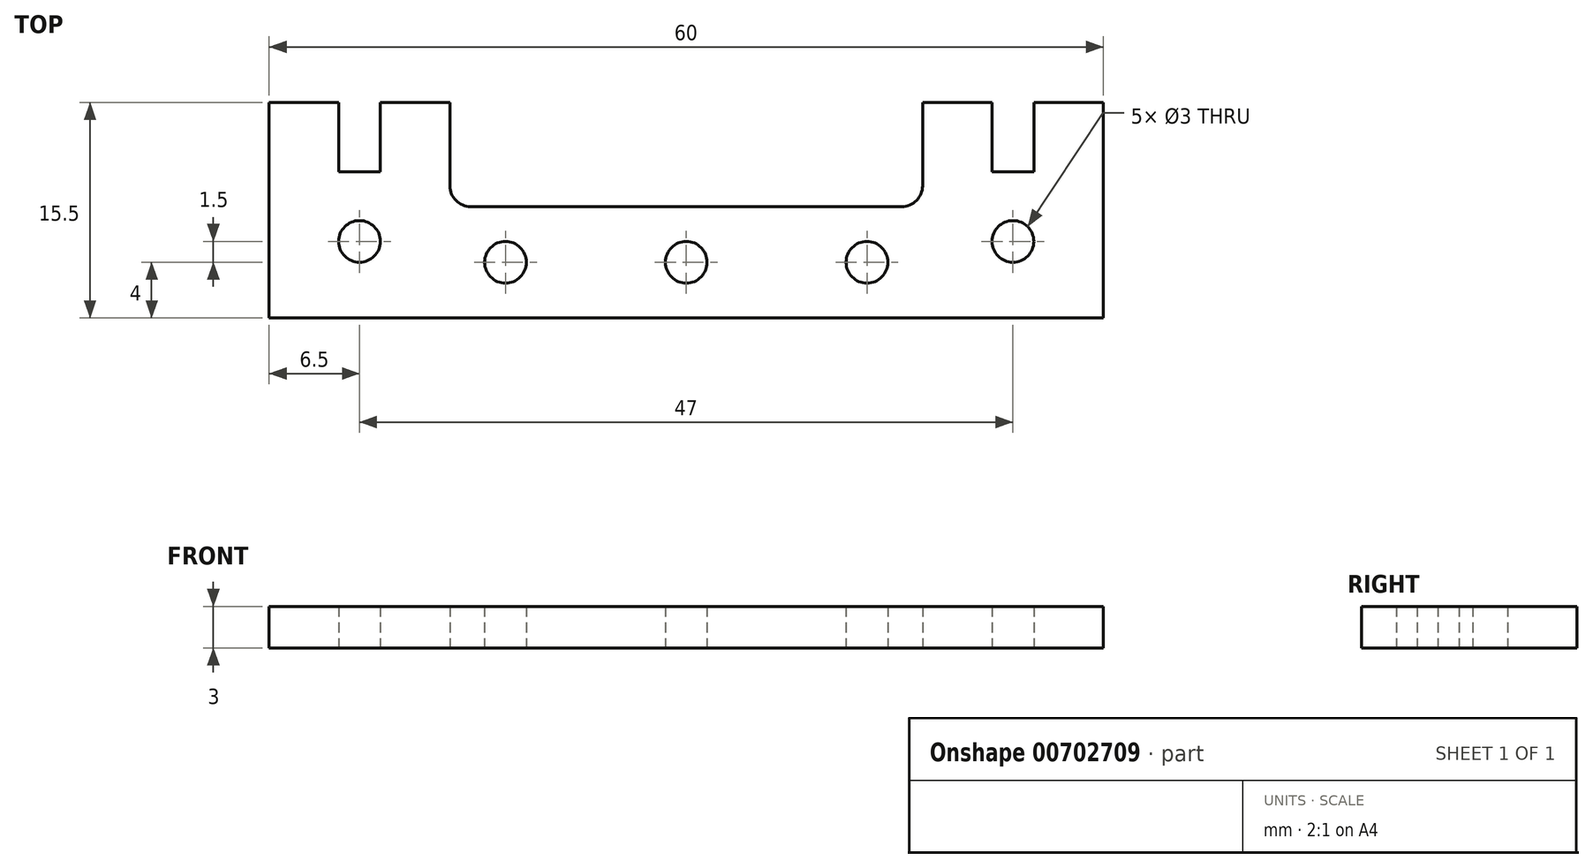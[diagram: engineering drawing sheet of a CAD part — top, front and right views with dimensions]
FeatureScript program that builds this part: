
annotation { "Feature Type Name" : "Feature", "Feature Type Description" : "" }
export const myFeature = defineFeature(function(context is Context, id is Id, definition is map)
    precondition{}
    {
        {
            var Q0;
            Q0=qCreatedBy(makeId("Top.planeOp"),FACE);
            var sketch = newSketch(context, id + "F0", { "sketchPlane" : qUnion([Q0])});
            skLineSegment(sketch, "E0.bottom", {"start": v(-30, 10) * mm, "end": v(-25, 10) * mm});
            skLineSegment(sketch, "E0.top", {"start": v(-30, -5.5) * mm, "end": v(30, -5.5) * mm});
            skLineSegment(sketch, "E0.left", {"start": v(-30, 10) * mm, "end": v(-30, -5.5) * mm});
            skLineSegment(sketch, "E0.right", {"start": v(30, 10) * mm, "end": v(30, -5.5) * mm});
            skLineSegment(sketch, "E1", {"start": v(0, 0) * mm, "end": v(0, -5.5) * mm, "construction": true});
            skCircle(sketch, "E2", {"center": v(0, -1.5) * mm, "radius": 1.5 * mm});
            skCircle(sketch, "E3", {"center": v(13, -1.5) * mm, "radius": 1.5 * mm});
            skCircle(sketch, "E4", {"center": v(-13, -1.5) * mm, "radius": 1.5 * mm});
            skLineSegment(sketch, "E5", {"start": v(25, 10) * mm, "end": v(25, 5) * mm});
            skLineSegment(sketch, "E6", {"start": v(25, 5) * mm, "end": v(22, 5) * mm});
            skLineSegment(sketch, "E7", {"start": v(22, 5) * mm, "end": v(22, 10) * mm});
            skLineSegment(sketch, "E8.MirrorCS", {"start": v(-22, 5) * mm, "end": v(-22, 10) * mm});
            skLineSegment(sketch, "E9.MirrorCS", {"start": v(-25, 10) * mm, "end": v(-25, 5) * mm});
            skLineSegment(sketch, "E10.MirrorCS", {"start": v(-25, 5) * mm, "end": v(-22, 5) * mm});
            skCircle(sketch, "E11", {"center": v(23.5, 0) * mm, "radius": 1.5 * mm});
            skPoint(sketch, "E11.centerSnap0", {"position": v(23.5, 5) * mm});
            skCircle(sketch, "E12.MirrorC", {"center": v(-23.5, 0) * mm, "radius": 1.5 * mm});
            skLineSegment(sketch, "E13.0", {"start": v(-15.5, 2.5) * mm, "end": v(15.5, 2.5) * mm});
            skLineSegment(sketch, "E14", {"start": v(17, 10) * mm, "end": v(17, 4) * mm});
            skLineSegment(sketch, "E15", {"start": v(-17, 10) * mm, "end": v(-17, 4) * mm});
            skLineSegment(sketch, "E16.trimOffspring", {"start": v(17, 10) * mm, "end": v(22, 10) * mm});
            skLineSegment(sketch, "E17.trimOffspring", {"start": v(-22, 10) * mm, "end": v(-17, 10) * mm});
            skLineSegment(sketch, "E18.trimOffspring", {"start": v(25, 10) * mm, "end": v(30, 10) * mm});
            skPoint(sketch, "E19.visualSharp", {"position": v(-17, 2.5) * mm});
            skArc(sketch, "E19.filletArc", {"start": v(-17, 4) * mm, "mid": v(-16.56, 2.94) * mm, "end": v(-15.5, 2.5) * mm});
            skPoint(sketch, "E20.visualSharp", {"position": v(17, 2.5) * mm});
            skArc(sketch, "E20.filletArc", {"start": v(15.5, 2.5) * mm, "mid": v(16.56, 2.94) * mm, "end": v(17, 4) * mm});
            skSolve(sketch);
        }
        {
            var Q0;
            {var subQ10=sQuery(id+"F0.wireOp",EDGE,"E0.left");Q0=makeQuery(id+"F0.imprint","IMPRINT",FACE,{"disambiguationData":[TD([[makeQuery(id+"F0.imprint","IMPRINT",EDGE,{"derivedFrom":subQ10}),1.0]])]});}
            extrude(context, id + "F1", {"entities" : qUnion([Q0]), "depth" : 3 * mm, "offsetDistance" : 25.4 * mm});
        }
    });
